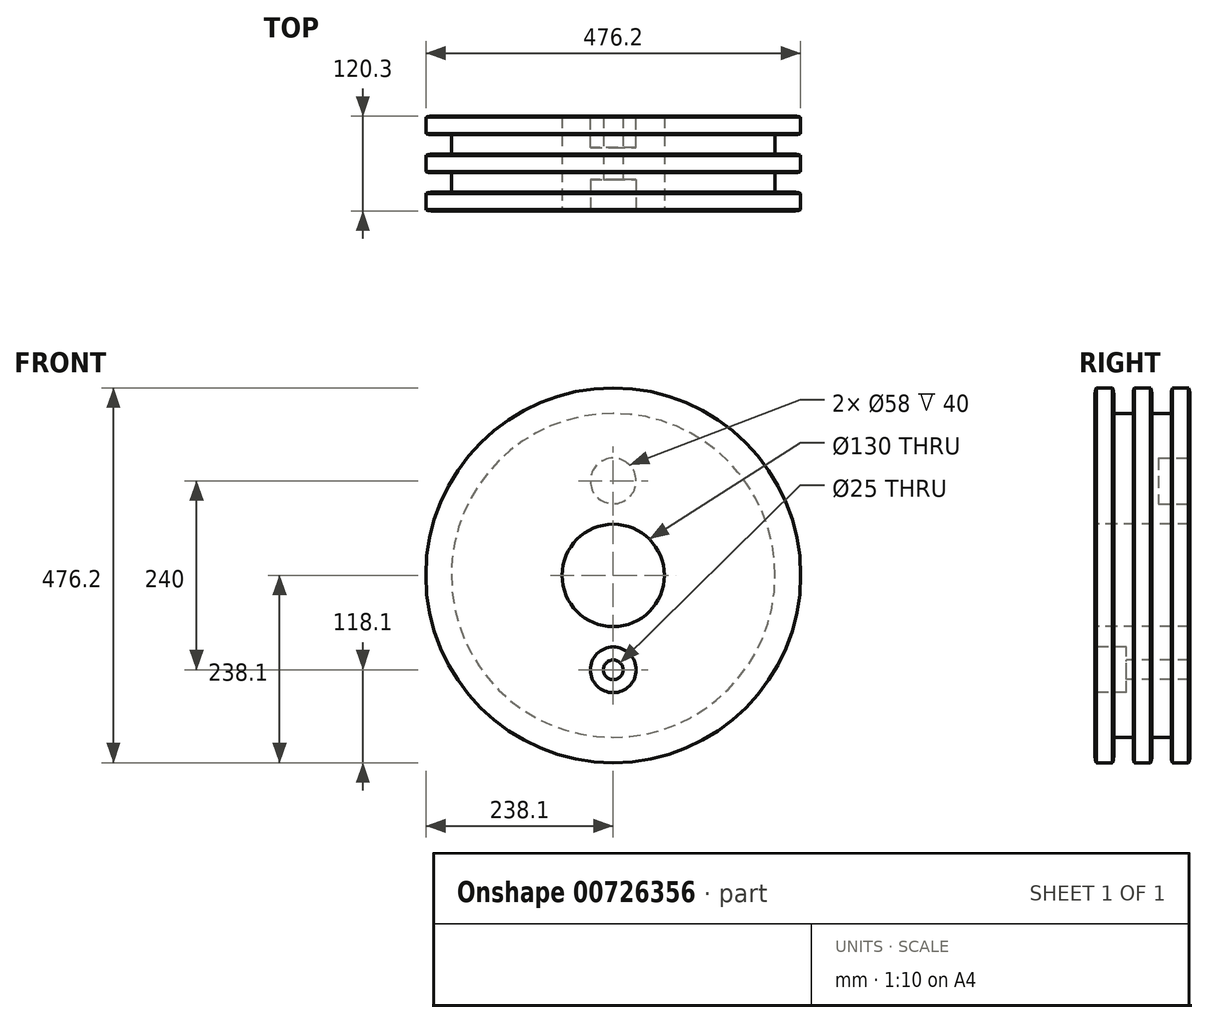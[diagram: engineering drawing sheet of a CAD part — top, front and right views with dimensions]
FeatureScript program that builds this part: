
annotation { "Feature Type Name" : "Feature", "Feature Type Description" : "" }
export const myFeature = defineFeature(function(context is Context, id is Id, definition is map)
    precondition{}
    {
        {
            var Q0;
            Q0=qCreatedBy(makeId("Front.planeOp"),FACE);
            var sketch = newSketch(context, id + "F0", { "sketchPlane" : qUnion([Q0])});
            skCircle(sketch, "E0", {"center": v(0, 0) * mm, "radius": 238.1 * mm});
            skSolve(sketch);
        }
        {
            var Q0;
            Q0=makeQuery(id+"F0.imprint","IMPRINT",FACE,{"disambiguationData":[TD([[makeQuery(id+"F0.imprint","IMPRINT",EDGE,{"derivedFrom":sQuery(id+"F0.wireOp",EDGE,"E0")}),1.0]])]});
            extrude(context, id + "F1", {"entities" : qUnion([Q0]), "depth" : (120.3 / 2) * mm, "offsetDistance" : 25.4 * mm, "hasSecondDirection" : true, "secondDirectionOppositeDirection" : true, "secondDirectionDepth" : (120.3 / 2) * mm});
        }
        {
            var Q0;
            Q0=makeQuery(id+"F1.opExtrude","CAP_FACE",FACE,{"disambiguationData":[OSD([sQuery(id+"F0.wireOp",EDGE,"E0")])],"isStart":false});
            var sketch = newSketch(context, id + "F2", { "sketchPlane" : qUnion([Q0])});
            skPoint(sketch, "E1", {"position": v(0, 0) * mm});
            skSolve(sketch);
        }
        {
            var Q0;
            Q0=sQuery(id+"F2.wireOp",VERTEX,"E1");
            var Q1;
            Q1=makeQuery(id+"F1.opExtrude","SWEPT_BODY",BODY,{"disambiguationData":[OSD([sQuery(id+"F0.wireOp",EDGE,"E0")])]});
            hole(context, id + "F3", {"style" : HoleStyle.SIMPLE, "endStyle" : HoleEndStyle.THROUGH, "holeDiameter" : 130 * mm, "majorDiameter" : 5 * mm, "isTappedThrough" : true, "tappedDepth" : 12 * mm, "tapClearance" : 3, "locations" : qUnion([Q0]), "scope" : qUnion([Q1])});
        }
        {
            var Q0;
            Q0=makeQuery(id+"F1.opExtrude","CAP_FACE",FACE,{"disambiguationData":[OSD([sQuery(id+"F0.wireOp",EDGE,"E0")])],"isStart":false});
            var sketch = newSketch(context, id + "F4", { "sketchPlane" : qUnion([Q0])});
            skCircle(sketch, "E2", {"center": v(0, 0) * mm, "radius": 120 * mm, "construction": true});
            skLineSegment(sketch, "E3", {"start": v(0, 150.87) * mm, "end": v(0, -165.36) * mm, "construction": true});
            skLineSegment(sketch, "E4", {"start": v(-159.15, 0) * mm, "end": v(157.08, 0) * mm, "construction": true});
            skPoint(sketch, "E5", {"position": v(0, -120) * mm});
            skCircle(sketch, "E6", {"center": v(0, 120) * mm, "radius": 29 * mm});
            skSolve(sketch);
        }
        {
            var Q0;
            Q0=sQuery(id+"F4.wireOp",VERTEX,"E5");
            var Q1;
            Q1=sQuery(id+"F4.wireOp",VERTEX,"81ab1e9d-935c-4c25-b5f3-d0e1429c5798.2.0");
            var Q2;
            Q2=sQuery(id+"F4.wireOp",VERTEX,"81ab1e9d-935c-4c25-b5f3-d0e1429c5798.1.0");
            var Q3;
            Q3=makeQuery(id+"F1.opExtrude","SWEPT_BODY",BODY,{"disambiguationData":[OSD([sQuery(id+"F0.wireOp",EDGE,"E0")])]});
            hole(context, id + "F5", {"style" : HoleStyle.C_BORE, "endStyle" : HoleEndStyle.THROUGH, "holeDiameter" : 25 * mm, "cBoreDiameter" : 58 * mm, "cBoreDepth" : 40 * mm, "majorDiameter" : 5 * mm, "isTappedThrough" : true, "tappedDepth" : 12 * mm, "tapClearance" : 3, "locations" : qUnion([Q0, Q1, Q2]), "scope" : qUnion([Q3])});
        }
        {
            var Q0;
            Q0=makeQuery(id+"F1.opExtrude","CAP_FACE",FACE,{"disambiguationData":[OSD([sQuery(id+"F0.wireOp",EDGE,"E0")])],"isStart":true});
            var sketch = newSketch(context, id + "F6", { "sketchPlane" : qUnion([Q0])});
            skCircle(sketch, "E7", {"center": v(0, 120) * mm, "radius": 29 * mm});
            skSolve(sketch);
        }
        {
            var Q0;
            Q0=makeQuery(id+"F6.imprint","IMPRINT",FACE,{"disambiguationData":[TD([[makeQuery(id+"F6.imprint","IMPRINT",EDGE,{"derivedFrom":sQuery(id+"F6.wireOp",EDGE,"E7")}),1.0]])]});
            extrude(context, id + "F7", {"entities" : qUnion([Q0]), "operationType" : NewBodyOperationType.REMOVE, "oppositeDirection" : true, "depth" : 40 * mm, "offsetDistance" : 25 * mm});
        }
        {
            var Q0;
            Q0=qCreatedBy(makeId("Right.planeOp"),FACE);
            var sketch = newSketch(context, id + "F8", { "sketchPlane" : qUnion([Q0])});
            skLineSegment(sketch, "E8.top", {"start": v(-11.8, 205.7) * mm, "end": v(-36.55, 205.7) * mm});
            skLineSegment(sketch, "E8.left", {"start": v(-11.8, 230.7) * mm, "end": v(-11.8, 205.7) * mm});
            skLineSegment(sketch, "E8.right", {"start": v(-36.55, 230.7) * mm, "end": v(-36.55, 205.7) * mm});
            skLineSegment(sketch, "E9.1.0.1", {"start": v(11.8, 230.7) * mm, "end": v(11.8, 205.7) * mm});
            skLineSegment(sketch, "E9.1.0.2", {"start": v(36.55, 230.7) * mm, "end": v(36.55, 205.7) * mm});
            skLineSegment(sketch, "E9.1.0.3", {"start": v(36.55, 205.7) * mm, "end": v(11.8, 205.7) * mm});
            skLineSegment(sketch, "E9.direction1", {"start": v(-36.55, 205.7) * mm, "end": v(11.8, 205.7) * mm, "construction": true});
            skLineSegment(sketch, "E10", {"start": v(38.05, 238.1) * mm, "end": v(58.65, 238.1) * mm});
            skLineSegment(sketch, "E11", {"start": v(60.15, 230.7) * mm, "end": v(60.15, 223.28) * mm});
            skLineSegment(sketch, "E12", {"start": v(60.15, 223.28) * mm, "end": v(86.06, 223.28) * mm});
            skLineSegment(sketch, "E13", {"start": v(86.06, 223.28) * mm, "end": v(86.06, 283.64) * mm});
            skLineSegment(sketch, "E14", {"start": v(86.06, 283.64) * mm, "end": v(-71.64, 283.64) * mm});
            skLineSegment(sketch, "E15", {"start": v(-71.64, 283.64) * mm, "end": v(-71.64, 224.88) * mm});
            skLineSegment(sketch, "E16", {"start": v(-71.64, 224.88) * mm, "end": v(-60.15, 224.88) * mm});
            skLineSegment(sketch, "E17", {"start": v(-60.15, 224.88) * mm, "end": v(-60.15, 238.1) * mm});
            skLineSegment(sketch, "E18", {"start": v(-58.65, 238.1) * mm, "end": v(-38.05, 238.1) * mm});
            skPoint(sketch, "E9.1.0.0.start.orphan", {"position": v(36.55, 270.51) * mm});
            skLineSegment(sketch, "E19", {"start": v(10.3, 238.1) * mm, "end": v(-10.3, 238.1) * mm});
            skPoint(sketch, "E20.orphan", {"position": v(11.8, 270.51) * mm});
            skPoint(sketch, "E21.orphan", {"position": v(-11.8, 270.51) * mm});
            skPoint(sketch, "E22", {"position": v(58.65, 238.1) * mm});
            skPoint(sketch, "E23", {"position": v(60.15, 230.7) * mm});
            skArc(sketch, "E24", {"start": v(60.15, 230.7) * mm, "mid": v(59.77, 234.47) * mm, "end": v(58.65, 238.1) * mm});
            skPoint(sketch, "E25.orphan", {"position": v(60.15, 238.1) * mm});
            skLineSegment(sketch, "E26", {"start": v(48.35, 207.9) * mm, "end": v(48.35, 250.36) * mm, "construction": true});
            skPoint(sketch, "E27.MirrorP", {"position": v(36.55, 230.7) * mm});
            skPoint(sketch, "E28.MirrorP", {"position": v(38.05, 238.1) * mm});
            skArc(sketch, "E29.MirrorCS", {"start": v(36.55, 230.7) * mm, "mid": v(36.93, 234.47) * mm, "end": v(38.05, 238.1) * mm});
            skPoint(sketch, "E30.MirrorP", {"position": v(36.55, 238.1) * mm});
            skPoint(sketch, "E31.1.0.0", {"position": v(-10.3, 238.1) * mm});
            skPoint(sketch, "E31.1.0.1", {"position": v(-11.8, 230.7) * mm});
            skPoint(sketch, "E31.1.0.2", {"position": v(11.8, 230.7) * mm});
            skPoint(sketch, "E31.1.0.3", {"position": v(11.8, 238.1) * mm});
            skPoint(sketch, "E31.1.0.4", {"position": v(-11.8, 238.1) * mm});
            skLineSegment(sketch, "E31.1.0.5", {"start": v(-10.3, 238.1) * mm, "end": v(10.3, 238.1) * mm});
            skArc(sketch, "E31.1.0.6", {"start": v(-11.8, 230.7) * mm, "mid": v(-11.42, 234.47) * mm, "end": v(-10.3, 238.1) * mm});
            skArc(sketch, "E31.1.0.7", {"start": v(11.8, 230.7) * mm, "mid": v(11.42, 234.47) * mm, "end": v(10.3, 238.1) * mm});
            skPoint(sketch, "E31.1.0.8", {"position": v(10.3, 238.1) * mm});
            skPoint(sketch, "E31.1.0.9", {"position": v(-11.8, 238.1) * mm});
            skPoint(sketch, "E31.2.0.0", {"position": v(-58.65, 238.1) * mm});
            skPoint(sketch, "E31.2.0.1", {"position": v(-60.15, 230.7) * mm});
            skPoint(sketch, "E31.2.0.2", {"position": v(-36.55, 230.7) * mm});
            skPoint(sketch, "E31.2.0.3", {"position": v(-36.55, 238.1) * mm});
            skPoint(sketch, "E31.2.0.4", {"position": v(-60.15, 238.1) * mm});
            skArc(sketch, "E31.2.0.6", {"start": v(-60.15, 230.7) * mm, "mid": v(-59.77, 234.47) * mm, "end": v(-58.65, 238.1) * mm});
            skArc(sketch, "E31.2.0.7", {"start": v(-36.55, 230.7) * mm, "mid": v(-36.93, 234.47) * mm, "end": v(-38.05, 238.1) * mm});
            skPoint(sketch, "E31.2.0.8", {"position": v(-38.05, 238.1) * mm});
            skPoint(sketch, "E31.2.0.9", {"position": v(-60.15, 238.1) * mm});
            skLineSegment(sketch, "E31.direction1", {"start": v(36.55, 230.7) * mm, "end": v(-11.8, 230.7) * mm, "construction": true});
            skSolve(sketch);
        }
        {
            var Q0;
            Q0 = qSketchRegion(id + "F8", true);
            var Q1;
            Q1=makeQuery(id+"F1.opExtrude","SWEPT_FACE",FACE,{"disambiguationData":[OSD([sQuery(id+"F0.wireOp",EDGE,"E0")])]});
            revolve(context, id + "F9", {"operationType" : NewBodyOperationType.REMOVE, "surfaceOperationType" : NewSurfaceOperationType.NEW, "entities" : qUnion([Q0]), "axis" : qUnion([Q1]), "revolveType" : RevolveType.FULL});
        }
    });
